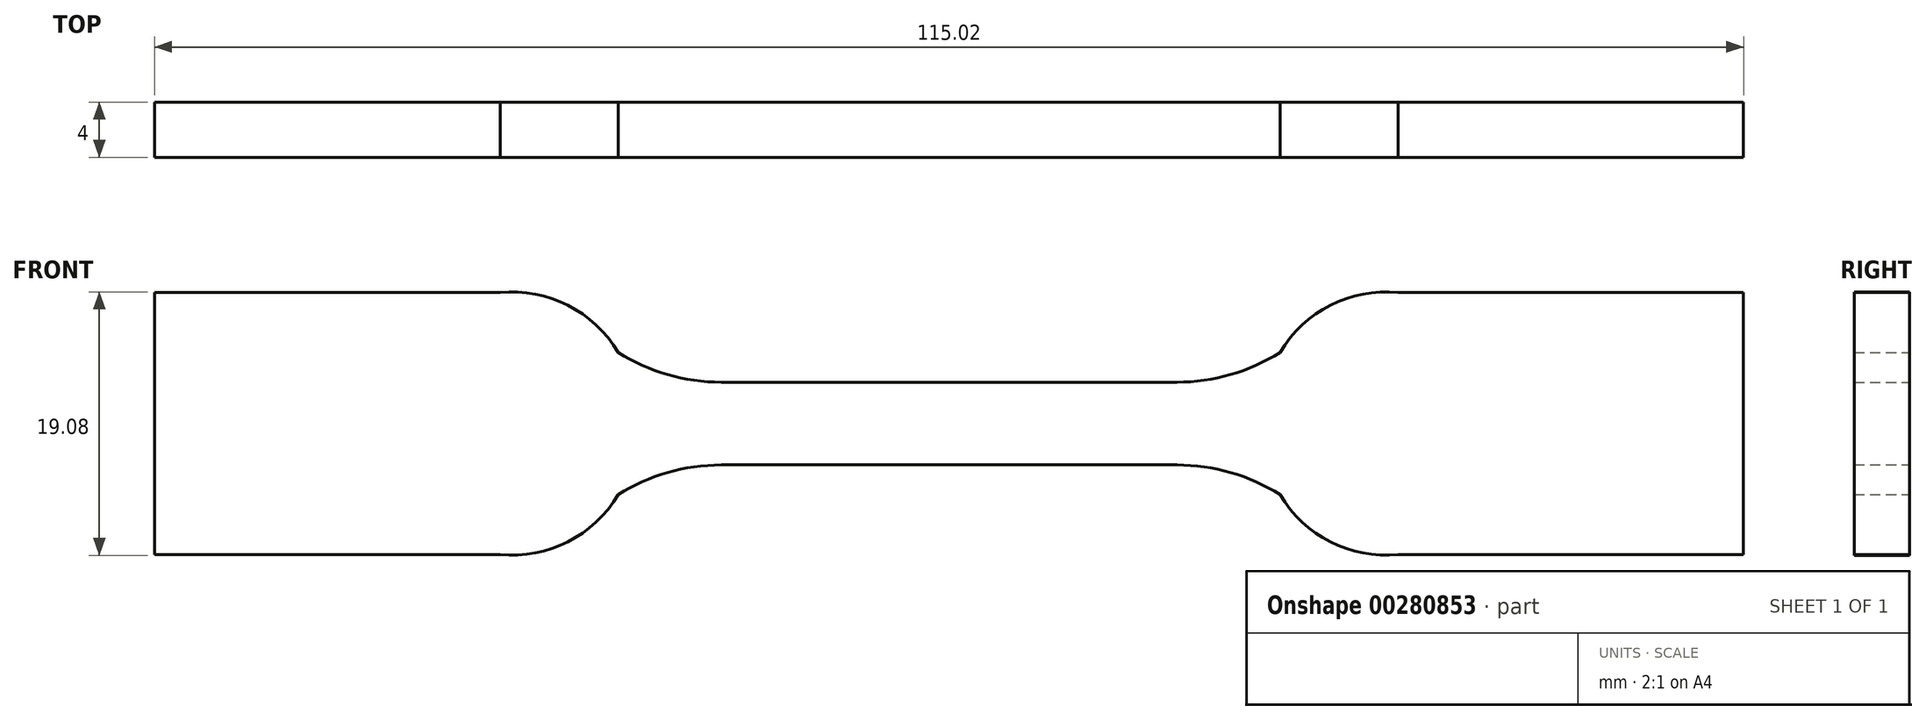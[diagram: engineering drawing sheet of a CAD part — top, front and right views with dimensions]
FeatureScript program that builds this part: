
annotation { "Feature Type Name" : "Feature", "Feature Type Description" : "" }
export const myFeature = defineFeature(function(context is Context, id is Id, definition is map)
    precondition{}
    {
        {
            var Q0;
            Q0=qCreatedBy(makeId("Front.planeOp"),FACE);
            var sketch = newSketch(context, id + "F0", { "sketchPlane" : qUnion([Q0])});
            skLineSegment(sketch, "E0", {"start": v(0, 3) * mm, "end": v(16.5, 3) * mm});
            skArc(sketch, "E1", {"start": v(16.5, 3) * mm, "mid": v(20.38, 3.55) * mm, "end": v(23.96, 5.15) * mm});
            skArc(sketch, "E2", {"start": v(32.5, 9.5) * mm, "mid": v(27.6, 8.57) * mm, "end": v(23.96, 5.15) * mm});
            skLineSegment(sketch, "E3", {"start": v(32.5, 9.5) * mm, "end": v(57.5, 9.5) * mm});
            skLineSegment(sketch, "E4", {"start": v(57.5, 9.5) * mm, "end": v(57.5, 0) * mm});
            skLineSegment(sketch, "E5.MirrorCS", {"start": v(0, -3) * mm, "end": v(16.5, -3) * mm});
            skLineSegment(sketch, "E6.MirrorCS", {"start": v(32.5, -9.5) * mm, "end": v(57.5, -9.5) * mm});
            skLineSegment(sketch, "E7.MirrorCS", {"start": v(57.5, -9.5) * mm, "end": v(57.5, 0) * mm});
            skArc(sketch, "E8.MirrorCS", {"start": v(32.5, -9.5) * mm, "mid": v(27.6, -8.57) * mm, "end": v(23.96, -5.15) * mm});
            skArc(sketch, "E9.MirrorCS", {"start": v(16.5, -3) * mm, "mid": v(20.38, -3.55) * mm, "end": v(23.96, -5.15) * mm});
            skArc(sketch, "E10.MirrorCS", {"start": v(-16.5, -3) * mm, "mid": v(-20.38, -3.55) * mm, "end": v(-23.96, -5.15) * mm});
            skArc(sketch, "E11.MirrorCS", {"start": v(-32.5, -9.5) * mm, "mid": v(-27.6, -8.57) * mm, "end": v(-23.96, -5.15) * mm});
            skLineSegment(sketch, "E12.MirrorCS", {"start": v(-57.5, -9.5) * mm, "end": v(-57.5, 0) * mm});
            skLineSegment(sketch, "E13.MirrorCS", {"start": v(0, 3) * mm, "end": v(-16.5, 3) * mm});
            skArc(sketch, "E14.MirrorCS", {"start": v(-16.5, 3) * mm, "mid": v(-20.38, 3.55) * mm, "end": v(-23.96, 5.15) * mm});
            skArc(sketch, "E15.MirrorCS", {"start": v(-32.5, 9.5) * mm, "mid": v(-27.6, 8.57) * mm, "end": v(-23.96, 5.15) * mm});
            skLineSegment(sketch, "E16.MirrorCS", {"start": v(0, -3) * mm, "end": v(-16.5, -3) * mm});
            skLineSegment(sketch, "E17.MirrorCS", {"start": v(-57.5, 9.5) * mm, "end": v(-57.5, 0) * mm});
            skLineSegment(sketch, "E18.MirrorCS", {"start": v(-32.5, 9.5) * mm, "end": v(-57.5, 9.5) * mm});
            skLineSegment(sketch, "E19.MirrorCS", {"start": v(-32.5, -9.5) * mm, "end": v(-57.5, -9.5) * mm});
            skSolve(sketch);
        }
        {
            var Q0;
            Q0 = qSketchRegion(id + "F0", true);
            extrude(context, id + "F1", {"entities" : qUnion([Q0]), "endBound" : BoundingType.SYMMETRIC, "depth" : 4 * mm});
        }
    });
